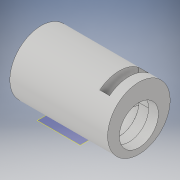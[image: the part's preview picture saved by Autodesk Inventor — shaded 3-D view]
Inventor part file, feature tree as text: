
AUTODESK INVENTOR PART (.ipt)
format: ipt  version: 2019 (Build 230136000, 136)  size: 268,288 bytes
history: native  units: in
note: dims shown in document units (in); Inventor stores cm internally (conversion verified against a paired STEP export)
features: sketch x9, extrude x4, revolve x1, loft x1, fillet x1, plane x1, other x1
ambient origin geometry x8: Origin, YZ Plane, XZ Plane, XY Plane, X Axis, Y Axis, Z Axis, Center Point
bodies: Solid1 (feature_tree)
feature tree (18):
  revolve  "Revolution1"  [1 undecoded]
  sketch  "Sketch2"  dims[d3=0.7874in d4=90.0deg]
  extrude  "Extrusion1"  TaperAngle=90.0deg  [1 undecoded]
  sketch  "Sketch4"  dims[d9=0.7874in d10=0.0in d11=90.0deg]
  sketch  "Sketch5"  dims[d12=0.0in d13=90.0deg d14=0.2362in]
  loft  "Loft1"
  fillet  "Fillet1"  Radius=0.3937in
  sketch  "Sketch6"  dims[d15=0.5118in d16=0.1969in d17=0.0in]
  plane  "Work Plane1"
  extrude  "Extrusion2"  TaperAngle=0.0deg  [1 undecoded]
  extrude  "Extrusion3"  Depth=0.2362in
  extrude  "Extrusion4"  Depth=0.1969in TaperAngle=0.0deg
  sketch  "Sketch1"  dims[d0=0.1181in d1=0.7874in]
  sketch  "Sketch3"  dims[d5=0.0591in d6=0.5118in d7=0.3937in d8=0.0in]
  other  "Edges1"
  sketch  "Sketch7"  dims[d18=0.6299in]
  sketch  "Sketch8"  dims[d19=0.7177in]
  sketch  "Sketch9"  dims[d22=0.3937in d24=0.1969in d25=0.0in d26=1.2598in d28=0.3937in d29=0.1199in d30=0.1969in d31=0.0in]
note: 3 required parameter values undecoded (feature->parameter linkage not recoverable at this tier; creation-order binding heuristic only, values carry confidence <= 0.55)